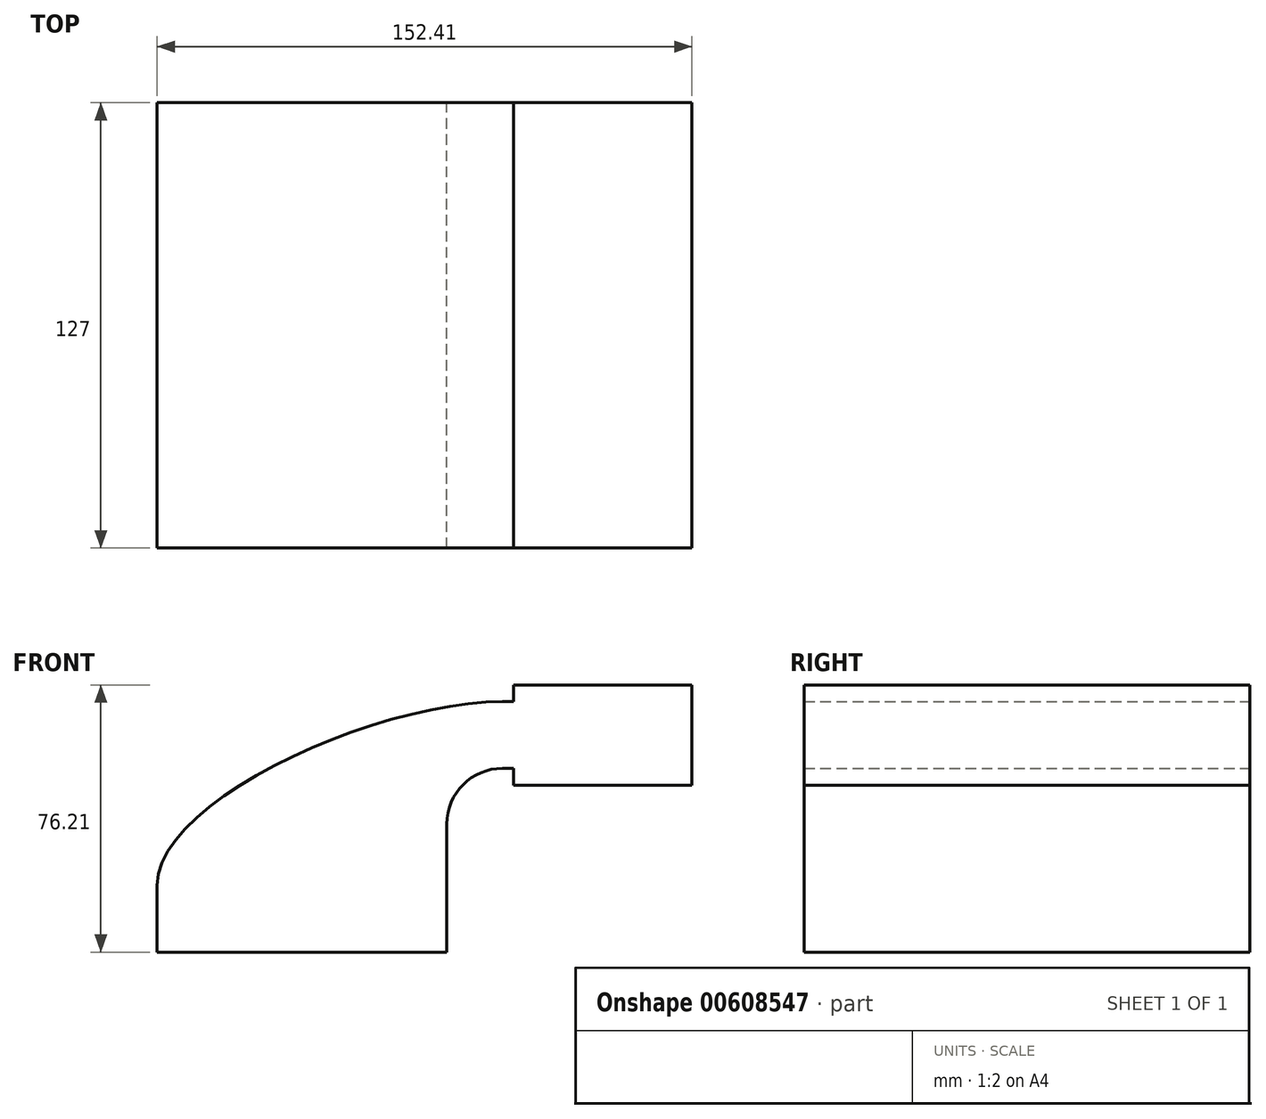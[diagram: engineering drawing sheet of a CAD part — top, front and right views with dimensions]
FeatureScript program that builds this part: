
annotation { "Feature Type Name" : "Feature", "Feature Type Description" : "" }
export const myFeature = defineFeature(function(context is Context, id is Id, definition is map)
    precondition{}
    {
        {
            var Q0;
            Q0=qCreatedBy(makeId("Front.planeOp"),FACE);
            var sketch = newSketch(context, id + "F0", { "sketchPlane" : qUnion([Q0])});
            skLineSegment(sketch, "E0.bottom", {"start": v(-41.28, 9.52) * mm, "end": v(41.27, 9.53) * mm});
            skLineSegment(sketch, "E0.top", {"start": v(-41.28, -9.53) * mm, "end": v(41.28, -9.53) * mm});
            skLineSegment(sketch, "E0.left", {"start": v(-41.28, 9.52) * mm, "end": v(-41.28, -9.53) * mm});
            skLineSegment(sketch, "E0.right", {"start": v(41.28, 9.53) * mm, "end": v(41.28, -9.52) * mm});
            skPoint(sketch, "E0.middle", {"position": v(0, 0) * mm});
            skLineSegment(sketch, "E1.bottom", {"start": v(111.12, 66.68) * mm, "end": v(60.32, 66.68) * mm});
            skLineSegment(sketch, "E1.top", {"start": v(111.12, 38.1) * mm, "end": v(60.32, 38.1) * mm});
            skLineSegment(sketch, "E1.left", {"start": v(111.12, 66.68) * mm, "end": v(111.12, 38.1) * mm});
            skLineSegment(sketch, "E1.right", {"start": v(60.32, 66.67) * mm, "end": v(60.32, 38.1) * mm});
            skPoint(sketch, "E1.middle", {"position": v(85.72, 52.39) * mm});
            skLineSegment(sketch, "E2", {"start": v(41.28, 9.53) * mm, "end": v(41.28, 27) * mm});
            skArc(sketch, "E3", {"start": v(41.27, 27) * mm, "mid": v(45.92, 38.23) * mm, "end": v(57.15, 42.88) * mm});
            skLineSegment(sketch, "E4", {"start": v(57.15, 42.88) * mm, "end": v(88.09, 42.88) * mm});
            skLineSegment(sketch, "E5.0", {"start": v(57.15, 61.93) * mm, "end": v(88.09, 61.93) * mm});
            skArc(sketch, "E5.1", {"start": v(22.22, 27) * mm, "mid": v(32.45, 51.7) * mm, "end": v(57.15, 61.93) * mm});
            skLineSegment(sketch, "E5.2", {"start": v(22.23, 9.61) * mm, "end": v(22.23, 27) * mm});
            skLineSegment(sketch, "E6", {"start": v(88.09, 66.68) * mm, "end": v(88.09, 38.1) * mm});
            skPoint(sketch, "E6.startSnap0", {"position": v(85.72, 66.68) * mm});
            skFitSpline(sketch, "E7", {"points": [v(-41.28, 9.53) * mm, v(57.15, 61.93) * mm], "startDerivative": vector(0, 73.4) * mm, "endDerivative": vector(106.26, 0) * mm});
            skSolve(sketch);
        }
        {
            var Q0;
            Q0 = qSketchRegion(id + "F0", true);
            extrude(context, id + "F1", {"entities" : qUnion([Q0]), "depth" : 127 * mm, "offsetDistance" : 25.4 * mm});
        }
    });
